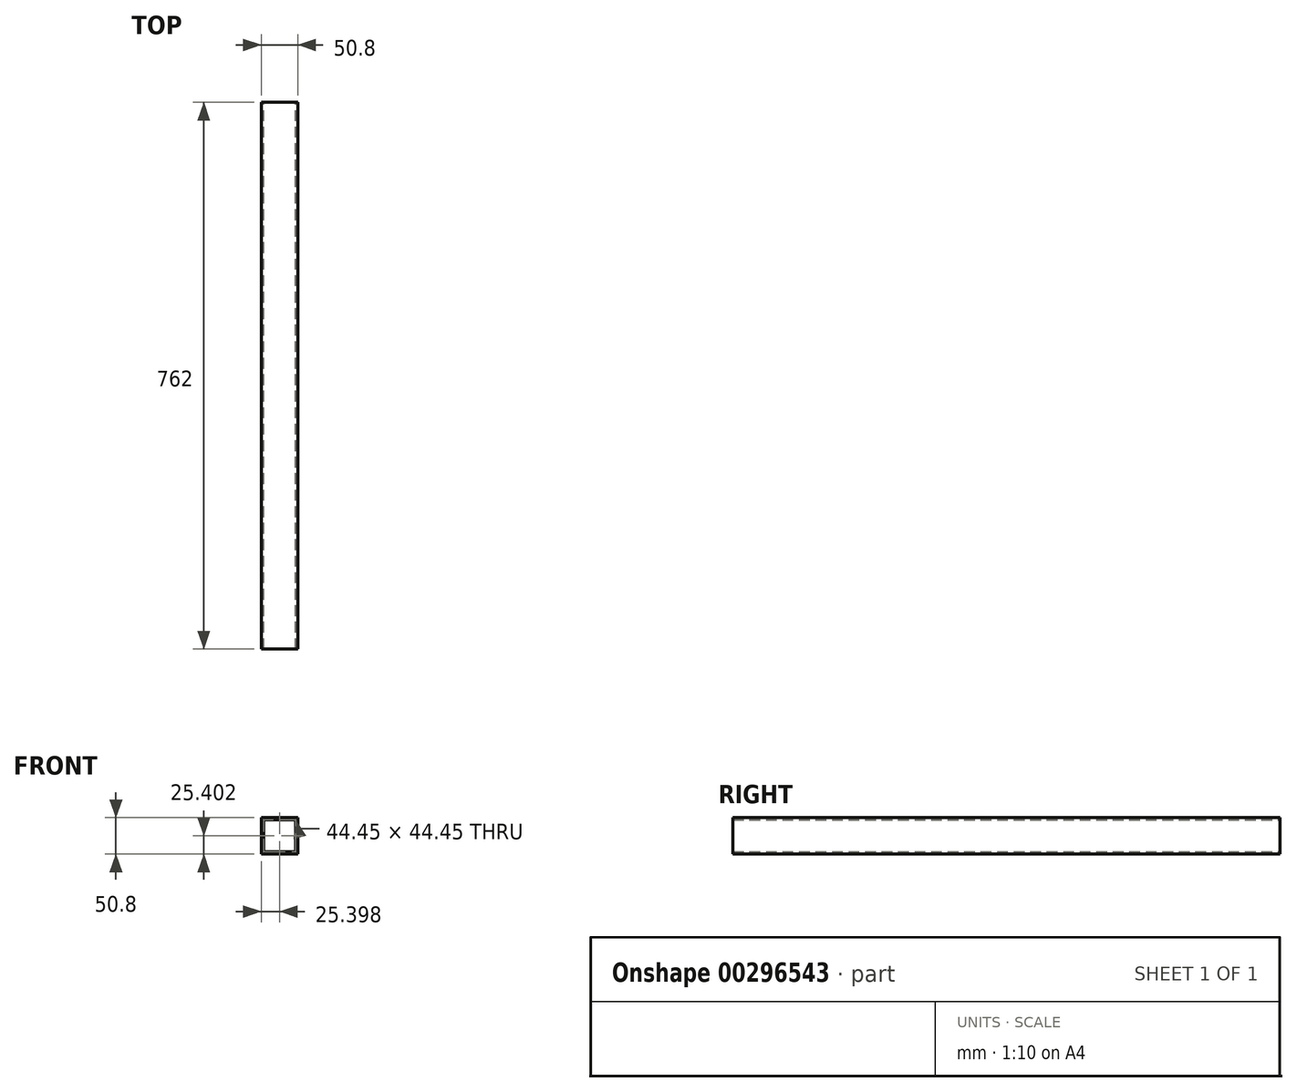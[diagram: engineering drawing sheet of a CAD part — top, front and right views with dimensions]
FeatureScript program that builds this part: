
annotation { "Feature Type Name" : "Feature", "Feature Type Description" : "" }
export const myFeature = defineFeature(function(context is Context, id is Id, definition is map)
    precondition{}
    {
        {
            var Q0;
            Q0=qCreatedBy(makeId("Front.planeOp"),FACE);
            var sketch = newSketch(context, id + "F0", { "sketchPlane" : qUnion([Q0])});
            skLineSegment(sketch, "E0.bottom", {"start": v(-74.25, 56.88) * mm, "end": v(-23.45, 56.88) * mm});
            skLineSegment(sketch, "E0.top", {"start": v(-74.25, 6.08) * mm, "end": v(-23.45, 6.08) * mm});
            skLineSegment(sketch, "E0.left", {"start": v(-74.25, 56.88) * mm, "end": v(-74.25, 6.08) * mm});
            skLineSegment(sketch, "E0.right", {"start": v(-23.45, 56.88) * mm, "end": v(-23.45, 6.08) * mm});
            skLineSegment(sketch, "E1.0", {"start": v(-71.08, 53.7) * mm, "end": v(-26.63, 53.7) * mm});
            skLineSegment(sketch, "E1.1", {"start": v(-71.08, 53.7) * mm, "end": v(-71.08, 9.26) * mm});
            skLineSegment(sketch, "E1.2", {"start": v(-71.08, 9.26) * mm, "end": v(-26.63, 9.26) * mm});
            skLineSegment(sketch, "E1.3", {"start": v(-26.63, 53.7) * mm, "end": v(-26.63, 9.26) * mm});
            skSolve(sketch);
        }
        {
            var Q0;
            Q0=makeQuery(id+"F0.imprint","IMPRINT",FACE,{"disambiguationData":[TD([[makeQuery(id+"F0.imprint","IMPRINT",EDGE,{"derivedFrom":sQuery(id+"F0.wireOp",EDGE,"E0.bottom")}),-1.0]])]});
            extrude(context, id + "F1", {"entities" : qUnion([Q0]), "depth" : 762 * mm});
        }
    });
